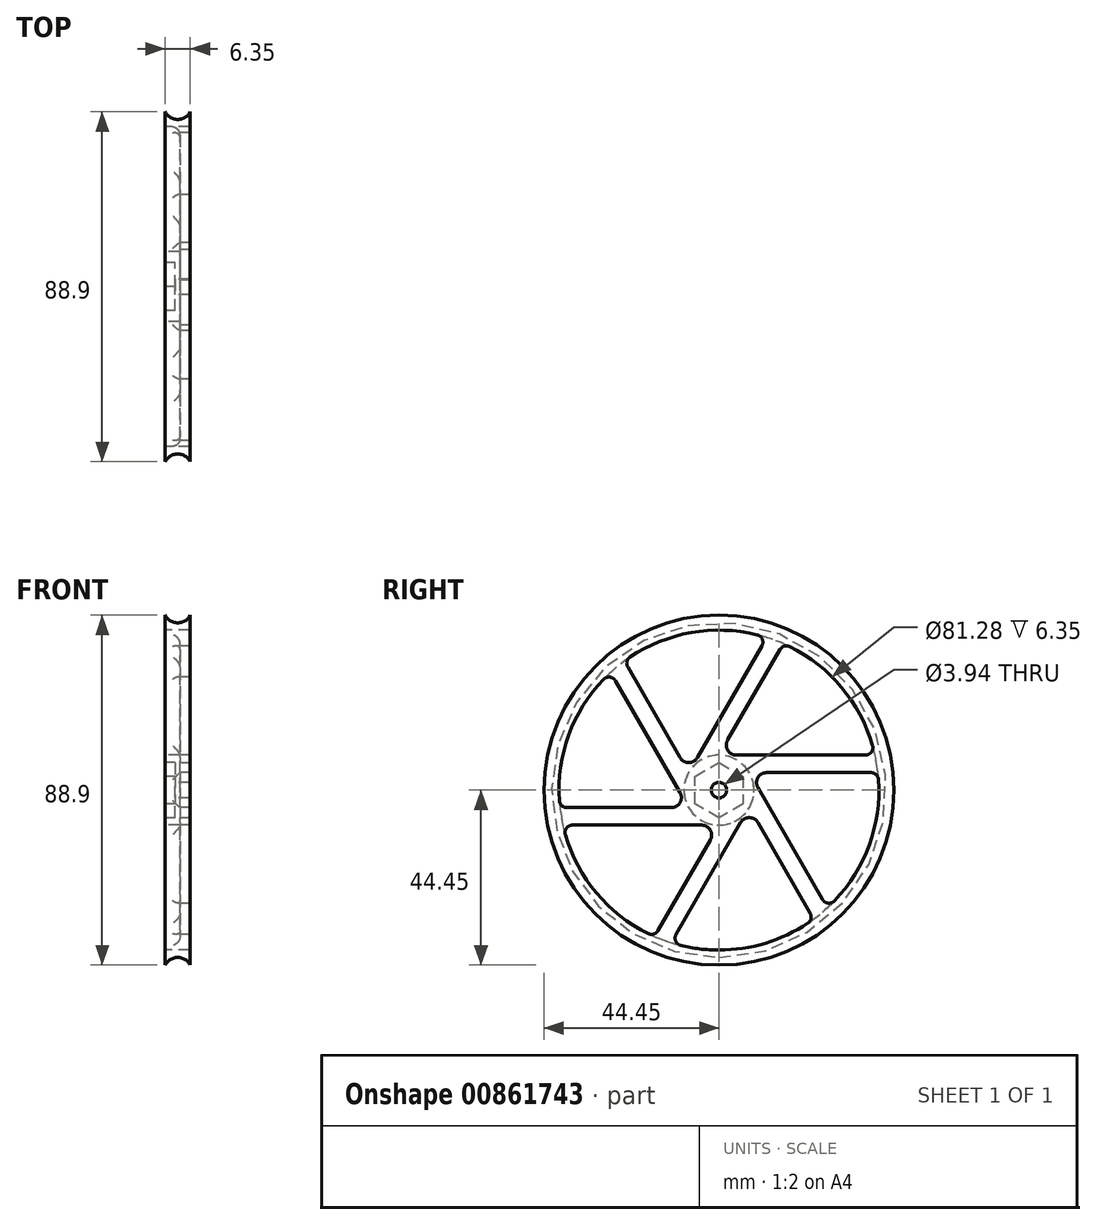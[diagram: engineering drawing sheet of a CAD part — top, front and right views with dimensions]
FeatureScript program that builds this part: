
annotation { "Feature Type Name" : "Feature", "Feature Type Description" : "" }
export const myFeature = defineFeature(function(context is Context, id is Id, definition is map)
    precondition{}
    {
        {
            var Q0;
            Q0=qCreatedBy(makeId("Front.planeOp"),FACE);
            var sketch = newSketch(context, id + "F0", { "sketchPlane" : qUnion([Q0])});
            skLineSegment(sketch, "E0", {"start": v(0, 0) * mm, "end": v(0, 44.45) * mm});
            skArc(sketch, "E1", {"start": v(0, 44.45) * mm, "mid": v(3.17, 42.5) * mm, "end": v(6.35, 44.45) * mm});
            skLineSegment(sketch, "E2", {"start": v(6.35, 44.45) * mm, "end": v(6.35, 40.64) * mm});
            skLineSegment(sketch, "E3", {"start": v(6.35, 40.64) * mm, "end": v(6.35, 0) * mm});
            skLineSegment(sketch, "E4", {"start": v(6.35, 0) * mm, "end": v(0, 0) * mm});
            skLineSegment(sketch, "E5", {"start": v(6.35, 0) * mm, "end": v(6.35, 8.9) * mm});
            skLineSegment(sketch, "E6", {"start": v(6.35, 8.9) * mm, "end": v(2.54, 8.9) * mm});
            skLineSegment(sketch, "E7", {"start": v(2.54, 8.9) * mm, "end": v(2.54, 40.64) * mm});
            skLineSegment(sketch, "E8", {"start": v(2.54, 40.64) * mm, "end": v(6.35, 40.64) * mm});
            skSolve(sketch);
        }
        {
            var Q0;
            Q0=makeQuery(id+"F0.imprint","IMPRINT",FACE,{"disambiguationData":[TD([[makeQuery(id+"F0.imprint","IMPRINT",EDGE,{"derivedFrom":sQuery(id+"F0.wireOp",EDGE,"E0")}),-1.0]])]});
            var Q1;
            Q1=sQuery(id+"F0.wireOp",EDGE,"E4");
            revolve(context, id + "F1", {"surfaceOperationType" : NewSurfaceOperationType.NEW, "entities" : qUnion([Q0]), "axis" : qUnion([Q1]), "revolveType" : RevolveType.FULL});
        }
        {
            var Q0;
            Q0=makeQuery(id+"F1.opRevolve","SWEPT_FACE",FACE,{"disambiguationData":[OSD([sQuery(id+"F0.wireOp",EDGE,"E3")])]});
            var sketch = newSketch(context, id + "F2", { "sketchPlane" : qUnion([Q0])});
            skCircle(sketch, "E9.cCircle", {"center": v(0, 0) * mm, "radius": 6.1 * mm, "construction": true});
            skLineSegment(sketch, "E9.0", {"start": v(6.1, 3.52) * mm, "end": v(6.1, -3.52) * mm});
            skLineSegment(sketch, "E9.1", {"start": v(6.1, -3.52) * mm, "end": v(0, -7.04) * mm});
            skLineSegment(sketch, "E9.2", {"start": v(0, -7.04) * mm, "end": v(-6.1, -3.52) * mm});
            skLineSegment(sketch, "E9.3", {"start": v(-6.1, -3.52) * mm, "end": v(-6.1, 3.52) * mm});
            skLineSegment(sketch, "E9.4", {"start": v(-6.1, 3.52) * mm, "end": v(0, 7.04) * mm});
            skLineSegment(sketch, "E9.5", {"start": v(0, 7.04) * mm, "end": v(6.1, 3.52) * mm});
            skPoint(sketch, "E9.0.midPoint", {"position": v(6.1, 0) * mm});
            skSolve(sketch);
        }
        {
            var Q0;
            Q0=makeQuery(id+"F2.imprint","IMPRINT",FACE,{"disambiguationData":[TD([[makeQuery(id+"F2.imprint","IMPRINT",EDGE,{"derivedFrom":sQuery(id+"F2.wireOp",EDGE,"E9.0")}),-1.0]])]});
            extrude(context, id + "F3", {"entities" : qUnion([Q0]), "operationType" : NewBodyOperationType.REMOVE, "oppositeDirection" : true, "depth" : 2.54 * mm, "offsetDistance" : 25.4 * mm});
        }
        {
            var Q0;
            Q0=makeQuery(id+"F1.opRevolve","SWEPT_FACE",FACE,{"disambiguationData":[OSD([sQuery(id+"F0.wireOp",EDGE,"E7")])]});
            var sketch = newSketch(context, id + "F4", { "sketchPlane" : qUnion([Q0])});
            skLineSegment(sketch, "E10", {"start": v(0, 8.9) * mm, "end": v(39.66, 8.9) * mm});
            skLineSegment(sketch, "E11", {"start": v(39.66, 8.9) * mm, "end": v(42.13, 8.9) * mm});
            skLineSegment(sketch, "E12", {"start": v(42.13, 8.9) * mm, "end": v(42.13, 4.45) * mm});
            skLineSegment(sketch, "E13", {"start": v(42.13, 4.45) * mm, "end": v(7.7, 4.45) * mm});
            skLineSegment(sketch, "E14.1.0", {"start": v(17.21, 38.7) * mm, "end": v(0, 8.9) * mm});
            skLineSegment(sketch, "E14.1.1", {"start": v(-7.7, 4.44) * mm, "end": v(12.13, 38.79) * mm});
            skLineSegment(sketch, "E14.2.0", {"start": v(-24.91, 34.26) * mm, "end": v(-7.7, 4.45) * mm});
            skLineSegment(sketch, "E14.2.1", {"start": v(-7.7, -4.45) * mm, "end": v(-27.53, 29.9) * mm});
            skLineSegment(sketch, "E14.3.0", {"start": v(-42.13, -4.45) * mm, "end": v(-7.7, -4.45) * mm});
            skLineSegment(sketch, "E14.3.1", {"start": v(0, -8.89) * mm, "end": v(-39.66, -8.9) * mm});
            skLineSegment(sketch, "E14.4.0", {"start": v(-17.21, -38.7) * mm, "end": v(0, -8.9) * mm});
            skLineSegment(sketch, "E14.4.1", {"start": v(7.7, -4.45) * mm, "end": v(-12.13, -38.79) * mm});
            skLineSegment(sketch, "E14.5.0", {"start": v(24.91, -34.26) * mm, "end": v(7.7, -4.45) * mm});
            skLineSegment(sketch, "E14.5.1", {"start": v(7.7, 4.45) * mm, "end": v(27.53, -29.9) * mm});
            skPoint(sketch, "E14.center", {"position": v(0, 0) * mm});
            skCircle(sketch, "E15", {"center": v(0, 0) * mm, "radius": 1.97 * mm});
            skSolve(sketch);
        }
        {
            var Q0;
            {var subQ0=sQuery(id+"F4.wireOp",EDGE,"E14.1.1");Q0=makeQuery(id+"F4.imprint","IMPRINT",FACE,{"disambiguationData":[TD([[makeQuery(id+"F4.imprint","IMPRINT",EDGE,{"derivedFrom":subQ0}),1.0]])]});}
            var Q1;
            {var subQ0=sQuery(id+"F4.wireOp",EDGE,"E10");Q1=makeQuery(id+"F4.imprint","IMPRINT",FACE,{"disambiguationData":[TD([[makeQuery(id+"F4.imprint","IMPRINT",EDGE,{"derivedFrom":subQ0}),1.0]])]});}
            var Q2;
            {var subQ6=sQuery(id+"F4.wireOp",EDGE,"E14.5.1");Q2=makeQuery(id+"F4.imprint","IMPRINT",FACE,{"disambiguationData":[TD([[makeQuery(id+"F4.imprint","IMPRINT",EDGE,{"derivedFrom":subQ6}),1.0]])]});}
            var Q3;
            {var subQ0=sQuery(id+"F4.wireOp",EDGE,"E14.4.1");Q3=makeQuery(id+"F4.imprint","IMPRINT",FACE,{"disambiguationData":[TD([[makeQuery(id+"F4.imprint","IMPRINT",EDGE,{"derivedFrom":subQ0}),1.0]])]});}
            var Q4;
            {var subQ0=sQuery(id+"F4.wireOp",EDGE,"E14.3.1");Q4=makeQuery(id+"F4.imprint","IMPRINT",FACE,{"disambiguationData":[TD([[makeQuery(id+"F4.imprint","IMPRINT",EDGE,{"derivedFrom":subQ0}),1.0]])]});}
            var Q5;
            {var subQ0=sQuery(id+"F4.wireOp",EDGE,"E14.2.1");Q5=makeQuery(id+"F4.imprint","IMPRINT",FACE,{"disambiguationData":[TD([[makeQuery(id+"F4.imprint","IMPRINT",EDGE,{"derivedFrom":subQ0}),1.0]])]});}
            extrude(context, id + "F5", {"entities" : qUnion([Q0, Q1, Q2, Q3, Q4, Q5]), "operationType" : NewBodyOperationType.REMOVE, "endBound" : BoundingType.THROUGH_ALL, "oppositeDirection" : true, "depth" : 25.4 * mm, "offsetDistance" : 25.4 * mm});
        }
        {
            var Q0;
            Q0=makeQuery(id+"F3.boolean.opBoolean","COPY",FACE,{"derivedFrom":makeQuery(id+"F3.opExtrude","CAP_FACE",FACE,{"disambiguationData":[OSD([sQuery(id+"F2.wireOp",EDGE,"E9.0"),sQuery(id+"F2.wireOp",EDGE,"E9.1"),sQuery(id+"F2.wireOp",EDGE,"E9.2"),sQuery(id+"F2.wireOp",EDGE,"E9.3"),sQuery(id+"F2.wireOp",EDGE,"E9.4"),sQuery(id+"F2.wireOp",EDGE,"E9.5")])],"isStart":false})});
            var sketch = newSketch(context, id + "F6", { "sketchPlane" : qUnion([Q0])});
            skCircle(sketch, "E16", {"center": v(0, 0) * mm, "radius": 1.97 * mm});
            skSolve(sketch);
        }
        {
            var Q0;
            Q0=makeQuery(id+"F6.imprint","IMPRINT",FACE,{"disambiguationData":[TD([[makeQuery(id+"F6.imprint","IMPRINT",EDGE,{"derivedFrom":sQuery(id+"F6.wireOp",EDGE,"E16")}),1.0]])]});
            extrude(context, id + "F7", {"entities" : qUnion([Q0]), "operationType" : NewBodyOperationType.REMOVE, "endBound" : BoundingType.THROUGH_ALL, "oppositeDirection" : true, "depth" : 25.4 * mm, "offsetDistance" : 25.4 * mm});
        }
        {
            var Q0;
            {var subQ0=sQuery(id+"F4.wireOp",EDGE,"E10");var subQ1=sQuery(id+"F0.wireOp",EDGE,"E8");var subQ3=sQuery(id+"F0.wireOp",EDGE,"E7");var subQ4=makeQuery(id+"F1.opRevolve","SWEPT_EDGE",EDGE,{"disambiguationData":[OSD([subQ3,subQ1])]});Q0=makeQuery(id+"F5.boolean.opBoolean","SPLIT",EDGE,{"disambiguationData":[TD([makeQuery(id+"F5.opExtrude","SWEPT_FACE",FACE,{"disambiguationData":[OSD([subQ0])]})])],"derivedFrom":subQ4});}
            var Q1;
            {var subQ0=sQuery(id+"F4.wireOp",EDGE,"E14.5.0");var subQ1=sQuery(id+"F0.wireOp",EDGE,"E8");var subQ3=sQuery(id+"F0.wireOp",EDGE,"E7");var subQ4=makeQuery(id+"F1.opRevolve","SWEPT_EDGE",EDGE,{"disambiguationData":[OSD([subQ3,subQ1])]});Q1=makeQuery(id+"F5.boolean.opBoolean","SPLIT",EDGE,{"disambiguationData":[TD([makeQuery(id+"F5.opExtrude","SWEPT_FACE",FACE,{"disambiguationData":[OSD([subQ0])]})])],"derivedFrom":subQ4});}
            var Q2;
            {var subQ1=sQuery(id+"F0.wireOp",EDGE,"E8");var subQ2=sQuery(id+"F4.wireOp",EDGE,"E14.4.0");var subQ3=sQuery(id+"F0.wireOp",EDGE,"E7");var subQ4=makeQuery(id+"F1.opRevolve","SWEPT_EDGE",EDGE,{"disambiguationData":[OSD([subQ3,subQ1])]});Q2=makeQuery(id+"F5.boolean.opBoolean","SPLIT",EDGE,{"disambiguationData":[TD([makeQuery(id+"F5.opExtrude","SWEPT_FACE",FACE,{"disambiguationData":[OSD([subQ2])]})])],"derivedFrom":subQ4});}
            var Q3;
            Q3=makeQuery(id+"F5.boolean.opBoolean","COPY",EDGE,{"derivedFrom":makeQuery(id+"F5.opExtrude","SWEPT_EDGE",EDGE,{"disambiguationData":[OSD([sQuery(id+"F0.wireOp",EDGE,"E7"),sQuery(id+"F0.wireOp",EDGE,"E8"),sQuery(id+"F4.wireOp",EDGE,"E14.4.1")])]})});
            var Q4;
            Q4=makeQuery(id+"F5.boolean.opBoolean","COPY",EDGE,{"derivedFrom":makeQuery(id+"F5.opExtrude","SWEPT_EDGE",EDGE,{"disambiguationData":[OSD([sQuery(id+"F0.wireOp",EDGE,"E7"),sQuery(id+"F0.wireOp",EDGE,"E8"),sQuery(id+"F4.wireOp",EDGE,"E10"),sQuery(id+"F4.wireOp",EDGE,"E11")])]})});
            var Q5;
            Q5=makeQuery(id+"F5.boolean.opBoolean","COPY",EDGE,{"derivedFrom":makeQuery(id+"F5.opExtrude","SWEPT_EDGE",EDGE,{"disambiguationData":[OSD([sQuery(id+"F0.wireOp",EDGE,"E7"),sQuery(id+"F0.wireOp",EDGE,"E8"),sQuery(id+"F4.wireOp",EDGE,"E14.5.0")])]})});
            var Q6;
            Q6=makeQuery(id+"F5.boolean.opBoolean","COPY",EDGE,{"derivedFrom":makeQuery(id+"F5.opExtrude","SWEPT_EDGE",EDGE,{"disambiguationData":[OSD([sQuery(id+"F0.wireOp",EDGE,"E7"),sQuery(id+"F0.wireOp",EDGE,"E8"),sQuery(id+"F4.wireOp",EDGE,"E14.4.0")])]})});
            var Q7;
            Q7=makeQuery(id+"F5.boolean.opBoolean","COPY",EDGE,{"derivedFrom":makeQuery(id+"F5.opExtrude","SWEPT_EDGE",EDGE,{"disambiguationData":[OSD([sQuery(id+"F0.wireOp",EDGE,"E7"),sQuery(id+"F0.wireOp",EDGE,"E8"),sQuery(id+"F4.wireOp",EDGE,"E14.5.1")])]})});
            var Q8;
            Q8=makeQuery(id+"F5.boolean.opBoolean","COPY",EDGE,{"derivedFrom":makeQuery(id+"F5.opExtrude","SWEPT_EDGE",EDGE,{"disambiguationData":[OSD([sQuery(id+"F0.wireOp",EDGE,"E7"),sQuery(id+"F0.wireOp",EDGE,"E8"),sQuery(id+"F4.wireOp",EDGE,"E14.2.0")])]})});
            var Q9;
            Q9=makeQuery(id+"F5.boolean.opBoolean","COPY",EDGE,{"derivedFrom":makeQuery(id+"F5.opExtrude","SWEPT_EDGE",EDGE,{"disambiguationData":[OSD([sQuery(id+"F0.wireOp",EDGE,"E7"),sQuery(id+"F0.wireOp",EDGE,"E8"),sQuery(id+"F4.wireOp",EDGE,"E14.3.0")])]})});
            var Q10;
            Q10=makeQuery(id+"F5.boolean.opBoolean","COPY",EDGE,{"derivedFrom":makeQuery(id+"F5.opExtrude","SWEPT_EDGE",EDGE,{"disambiguationData":[OSD([sQuery(id+"F0.wireOp",EDGE,"E7"),sQuery(id+"F0.wireOp",EDGE,"E8"),sQuery(id+"F4.wireOp",EDGE,"E14.1.0")])]})});
            var Q11;
            Q11=makeQuery(id+"F5.boolean.opBoolean","COPY",EDGE,{"derivedFrom":makeQuery(id+"F5.opExtrude","SWEPT_EDGE",EDGE,{"disambiguationData":[OSD([sQuery(id+"F0.wireOp",EDGE,"E7"),sQuery(id+"F0.wireOp",EDGE,"E8"),sQuery(id+"F4.wireOp",EDGE,"E14.3.1")])]})});
            var Q12;
            Q12=makeQuery(id+"F5.boolean.opBoolean","COPY",EDGE,{"derivedFrom":makeQuery(id+"F5.opExtrude","SWEPT_EDGE",EDGE,{"disambiguationData":[OSD([sQuery(id+"F0.wireOp",EDGE,"E7"),sQuery(id+"F0.wireOp",EDGE,"E8"),sQuery(id+"F4.wireOp",EDGE,"E14.2.1")])]})});
            var Q13;
            Q13=makeQuery(id+"F5.boolean.opBoolean","COPY",EDGE,{"derivedFrom":makeQuery(id+"F5.opExtrude","SWEPT_EDGE",EDGE,{"disambiguationData":[OSD([sQuery(id+"F0.wireOp",EDGE,"E7"),sQuery(id+"F0.wireOp",EDGE,"E8"),sQuery(id+"F4.wireOp",EDGE,"E13")])]})});
            var Q14;
            {var subQ1=sQuery(id+"F0.wireOp",EDGE,"E8");var subQ2=sQuery(id+"F0.wireOp",EDGE,"E7");var subQ3=makeQuery(id+"F1.opRevolve","SWEPT_EDGE",EDGE,{"disambiguationData":[OSD([subQ2,subQ1])]});var subQ4=sQuery(id+"F4.wireOp",EDGE,"E14.3.0");Q14=makeQuery(id+"F5.boolean.opBoolean","SPLIT",EDGE,{"disambiguationData":[TD([makeQuery(id+"F5.opExtrude","SWEPT_FACE",FACE,{"disambiguationData":[OSD([subQ4])]})])],"derivedFrom":subQ3});}
            var Q15;
            {var subQ1=sQuery(id+"F0.wireOp",EDGE,"E8");var subQ2=sQuery(id+"F4.wireOp",EDGE,"E14.2.0");var subQ3=sQuery(id+"F0.wireOp",EDGE,"E7");var subQ4=makeQuery(id+"F1.opRevolve","SWEPT_EDGE",EDGE,{"disambiguationData":[OSD([subQ3,subQ1])]});Q15=makeQuery(id+"F5.boolean.opBoolean","SPLIT",EDGE,{"disambiguationData":[TD([makeQuery(id+"F5.opExtrude","SWEPT_FACE",FACE,{"disambiguationData":[OSD([subQ2])]})])],"derivedFrom":subQ4});}
            var Q16;
            Q16=makeQuery(id+"F5.boolean.opBoolean","COPY",EDGE,{"derivedFrom":makeQuery(id+"F5.opExtrude","SWEPT_EDGE",EDGE,{"disambiguationData":[OSD([sQuery(id+"F0.wireOp",EDGE,"E7"),sQuery(id+"F0.wireOp",EDGE,"E8"),sQuery(id+"F4.wireOp",EDGE,"E14.1.1")])]})});
            var Q17;
            {var subQ1=sQuery(id+"F0.wireOp",EDGE,"E8");var subQ2=sQuery(id+"F0.wireOp",EDGE,"E7");var subQ3=makeQuery(id+"F1.opRevolve","SWEPT_EDGE",EDGE,{"disambiguationData":[OSD([subQ2,subQ1])]});var subQ4=sQuery(id+"F4.wireOp",EDGE,"E14.1.0");Q17=makeQuery(id+"F5.boolean.opBoolean","SPLIT",EDGE,{"disambiguationData":[TD([makeQuery(id+"F5.opExtrude","SWEPT_FACE",FACE,{"disambiguationData":[OSD([subQ4])]})])],"derivedFrom":subQ3});}
            fillet(context, id + "F8", {"entities" : qUnion([Q0, Q1, Q2, Q3, Q4, Q5, Q6, Q7, Q8, Q9, Q10, Q11, Q12, Q13, Q14, Q15, Q16, Q17]), "radius" : 1.9 * mm, "tangentPropagation" : true, "allowEdgeOverflow" : false});
        }
        {
            var Q0;
            Q0=makeQuery(id+"F5.boolean.opBoolean","COPY",EDGE,{"derivedFrom":makeQuery(id+"F5.opExtrude","SWEPT_EDGE",EDGE,{"disambiguationData":[OSD([sQuery(id+"F0.wireOp",EDGE,"E6"),sQuery(id+"F0.wireOp",EDGE,"E7"),sQuery(id+"F4.wireOp",EDGE,"E14.4.1"),sQuery(id+"F4.wireOp",EDGE,"E14.5.0")])]})});
            var Q1;
            Q1=makeQuery(id+"F5.boolean.opBoolean","COPY",EDGE,{"derivedFrom":makeQuery(id+"F5.opExtrude","SWEPT_EDGE",EDGE,{"disambiguationData":[OSD([sQuery(id+"F0.wireOp",EDGE,"E6"),sQuery(id+"F0.wireOp",EDGE,"E7"),sQuery(id+"F4.wireOp",EDGE,"E14.3.1"),sQuery(id+"F4.wireOp",EDGE,"E14.4.0")])]})});
            var Q2;
            Q2=makeQuery(id+"F5.boolean.opBoolean","COPY",EDGE,{"derivedFrom":makeQuery(id+"F5.opExtrude","SWEPT_EDGE",EDGE,{"disambiguationData":[OSD([sQuery(id+"F0.wireOp",EDGE,"E6"),sQuery(id+"F0.wireOp",EDGE,"E7"),sQuery(id+"F4.wireOp",EDGE,"E14.2.1"),sQuery(id+"F4.wireOp",EDGE,"E14.3.0")])]})});
            var Q3;
            Q3=makeQuery(id+"F5.boolean.opBoolean","COPY",EDGE,{"derivedFrom":makeQuery(id+"F5.opExtrude","SWEPT_EDGE",EDGE,{"disambiguationData":[OSD([sQuery(id+"F0.wireOp",EDGE,"E6"),sQuery(id+"F0.wireOp",EDGE,"E7"),sQuery(id+"F4.wireOp",EDGE,"E14.1.1"),sQuery(id+"F4.wireOp",EDGE,"E14.2.0")])]})});
            var Q4;
            Q4=makeQuery(id+"F5.boolean.opBoolean","COPY",EDGE,{"derivedFrom":makeQuery(id+"F5.opExtrude","SWEPT_EDGE",EDGE,{"disambiguationData":[OSD([sQuery(id+"F0.wireOp",EDGE,"E6"),sQuery(id+"F0.wireOp",EDGE,"E7"),sQuery(id+"F4.wireOp",EDGE,"E10"),sQuery(id+"F4.wireOp",EDGE,"E14.1.0")])]})});
            var Q5;
            Q5=makeQuery(id+"F5.boolean.opBoolean","COPY",EDGE,{"derivedFrom":makeQuery(id+"F5.opExtrude","SWEPT_EDGE",EDGE,{"disambiguationData":[OSD([sQuery(id+"F0.wireOp",EDGE,"E6"),sQuery(id+"F0.wireOp",EDGE,"E7"),sQuery(id+"F4.wireOp",EDGE,"E13"),sQuery(id+"F4.wireOp",EDGE,"E14.5.1")])]})});
            fillet(context, id + "F9", {"entities" : qUnion([Q0, Q1, Q2, Q3, Q4, Q5]), "radius" : 2.54 * mm, "tangentPropagation" : true, "allowEdgeOverflow" : false});
        }
        {
            var Q0;
            Q0=makeQuery(id+"F1.opRevolve","SWEPT_BODY",BODY,{"disambiguationData":[OSD([sQuery(id+"F0.wireOp",EDGE,"E0"),sQuery(id+"F0.wireOp",EDGE,"E1"),sQuery(id+"F0.wireOp",EDGE,"E2"),sQuery(id+"F0.wireOp",EDGE,"E3"),sQuery(id+"F0.wireOp",EDGE,"E4"),sQuery(id+"F0.wireOp",EDGE,"E6"),sQuery(id+"F0.wireOp",EDGE,"E7"),sQuery(id+"F0.wireOp",EDGE,"E8")])]});
            var Q1;
            Q1=makeQuery(id+"F1.opRevolve","SWEPT_FACE",FACE,{"disambiguationData":[OSD([sQuery(id+"F0.wireOp",EDGE,"E0")])]});
            mirror(context, id + "F10", {"entities" : qUnion([Q0]), "mirrorPlane" : qUnion([Q1])});
        }
        {
            var Q0;
            Q0=makeQuery(id+"F1.opRevolve","SWEPT_BODY",BODY,{"disambiguationData":[OSD([sQuery(id+"F0.wireOp",EDGE,"E0"),sQuery(id+"F0.wireOp",EDGE,"E1"),sQuery(id+"F0.wireOp",EDGE,"E2"),sQuery(id+"F0.wireOp",EDGE,"E3"),sQuery(id+"F0.wireOp",EDGE,"E4"),sQuery(id+"F0.wireOp",EDGE,"E6"),sQuery(id+"F0.wireOp",EDGE,"E7"),sQuery(id+"F0.wireOp",EDGE,"E8")])]});
            deleteBodies(context, id + "F11", {"entities" : qUnion([Q0])});
        }
    });
